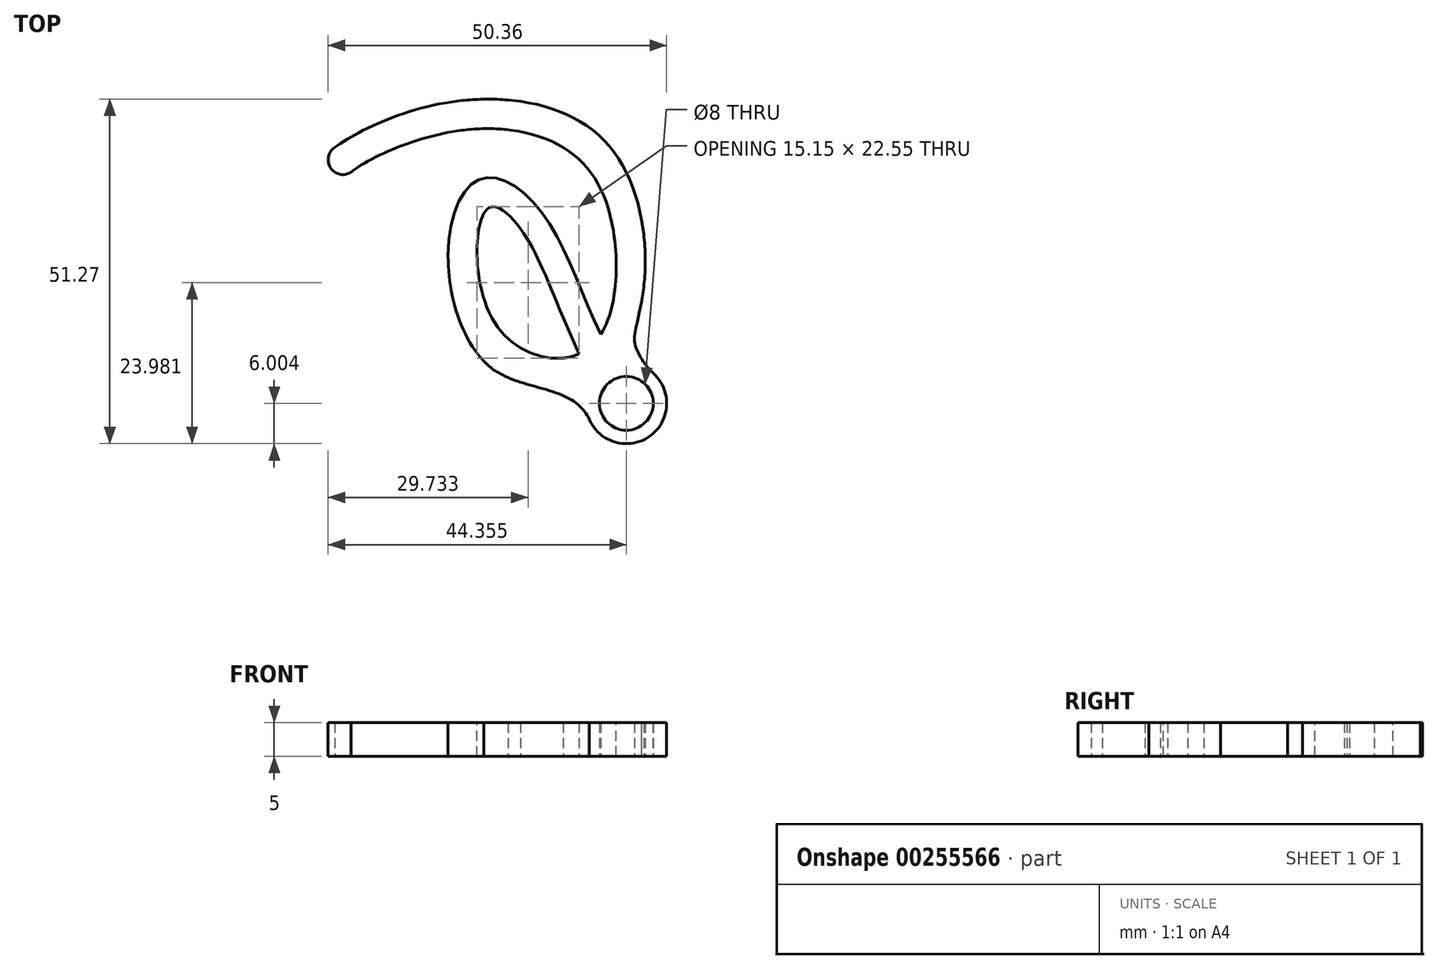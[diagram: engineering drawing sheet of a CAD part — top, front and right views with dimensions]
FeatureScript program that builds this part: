
annotation { "Feature Type Name" : "Feature", "Feature Type Description" : "" }
export const myFeature = defineFeature(function(context is Context, id is Id, definition is map)
    precondition{}
    {
        {
            var Q0;
            Q0=qCreatedBy(makeId("Front.planeOp"),FACE);
            var sketch = newSketch(context, id + "F0", { "sketchPlane" : qUnion([Q0])});
            skFitSpline(sketch, "E0", {"points": [v(-7.64, -32.72) * mm, v(-14.39, -18.66) * mm, v(-19.1, -15.72) * mm, v(-18.72, -31.73) * mm, v(-7.64, -37.97) * mm, v(-1.29, -32.33) * mm, v(-1.18, -15.7) * mm, v(-8.44, -6.5) * mm, v(-24.35, -4.3) * mm, v(-39.48, -10.34) * mm], "startDerivative": vector(-66.54, 155.96) * mm, "endDerivative": vector(-60.32, -50) * mm});
            skLineSegment(sketch, "E1", {"start": v(-8.07, -31.71) * mm, "end": v(-5.6, -37.39) * mm});
            skFitSpline(sketch, "E2", {"points": [v(-2.33, -34.44) * mm, v(-10.87, -16.7) * mm, v(-19.4, -11.15) * mm, v(-24.68, -18.43) * mm, v(-19.74, -38.45) * mm, v(-5, -41.52) * mm, v(3.68, -29.5) * mm, v(-1.85, -5.62) * mm, v(-25.4, 0) * mm, v(-41.93, -6.67) * mm], "startDerivative": vector(-78.74, 155.85) * mm, "endDerivative": vector(-78.56, -57.77) * mm});
            skLineSegment(sketch, "E3", {"start": v(-39.48, -10.34) * mm, "end": v(-41.93, -6.67) * mm});
            skCircle(sketch, "E4", {"center": v(-40.7, -8.5) * mm, "radius": 2.2 * mm});
            skSolve(sketch);
        }
        {
            var Q0;
            Q0=qCreatedBy(makeId("Top.planeOp"),FACE);
            var sketch = newSketch(context, id + "F1", { "sketchPlane" : qUnion([Q0])});
            skFitSpline(sketch, "E5", {"points": [v(14.78, -14.43) * mm, v(8.03, -0.37) * mm, v(3.33, 2.57) * mm, v(3.7, -13.44) * mm, v(14.78, -19.68) * mm, v(21.12, -14.03) * mm, v(21.16, 2.56) * mm, v(14.01, 11.88) * mm, v(-1.94, 13.98) * mm, v(-17.06, 7.95) * mm], "startDerivative": vector(-66.54, 155.96) * mm, "endDerivative": vector(-60.36, -49.94) * mm});
            skLineSegment(sketch, "E6", {"start": v(14.46, -13.68) * mm, "end": v(16.82, -19.1) * mm});
            skFitSpline(sketch, "E7", {"points": [v(20.09, -16.15) * mm, v(11.55, 1.6) * mm, v(3.01, 7.13) * mm, v(-2.26, -0.14) * mm, v(2.68, -20.15) * mm, v(17.42, -23.23) * mm, v(26.13, -11.2) * mm, v(20.6, 12.64) * mm, v(-3, 18.27) * mm, v(-19.5, 11.62) * mm], "startDerivative": vector(-78.74, 155.85) * mm, "endDerivative": vector(-78.48, -57.87) * mm});
            skLineSegment(sketch, "E8", {"start": v(-17.06, 7.95) * mm, "end": v(-19.5, 11.62) * mm});
            skCircle(sketch, "E9", {"center": v(-18.28, 9.79) * mm, "radius": 2.2 * mm});
            skLineSegment(sketch, "E10", {"start": v(4, 2.8) * mm, "end": v(13.82, -19.75) * mm});
            skLineSegment(sketch, "E11", {"start": v(-3, 18.27) * mm, "end": v(-1.94, 13.98) * mm});
            skLineSegment(sketch, "E12", {"start": v(6.27, 18.68) * mm, "end": v(8.13, 18.47) * mm});
            skLineSegment(sketch, "E13", {"start": v(7.2, 18.58) * mm, "end": v(6.7, 14.2) * mm});
            skLineSegment(sketch, "E14", {"start": v(26.1, 0.98) * mm, "end": v(26.45, -1.27) * mm});
            skLineSegment(sketch, "E15", {"start": v(26.3, -0.15) * mm, "end": v(21.94, -0.82) * mm});
            skPoint(sketch, "E15.startSnap0", {"position": v(26.28, -0.15) * mm});
            skLineSegment(sketch, "E16", {"start": v(16.82, -19.1) * mm, "end": v(18.42, -22.8) * mm});
            skLineSegment(sketch, "E17", {"start": v(-17.06, 7.95) * mm, "end": v(18.42, -22.8) * mm});
            skLineSegment(sketch, "E18", {"start": v(20.09, -16.15) * mm, "end": v(21.87, -20.23) * mm});
            skLineSegment(sketch, "E19", {"start": v(20.28, -21.64) * mm, "end": v(23.87, -26.46) * mm});
            skCircle(sketch, "E20", {"center": v(23.87, -26.46) * mm, "radius": 6 * mm});
            skFitSpline(sketch, "E21", {"points": [v(2.68, -20.15) * mm, v(13.87, -25.05) * mm, v(18.35, -28.82) * mm], "startDerivative": vector(13.57, -15.72) * mm, "endDerivative": vector(5.37, -11.86) * mm});
            skFitSpline(sketch, "E22", {"points": [v(27.79, -21.92) * mm, v(25.16, -17.6) * mm, v(26.13, -11.2) * mm], "startDerivative": vector(-9.12, 8.94) * mm, "endDerivative": vector(4.13, 22.33) * mm});
            skCircle(sketch, "E23", {"center": v(23.87, -26.46) * mm, "radius": 4 * mm});
            skSolve(sketch);
        }
        {
            var Q0;
            {var subQ0=sQuery(id+"F1.wireOp",EDGE,"E8");Q0=makeQuery(id+"F1.imprint","IMPRINT",FACE,{"disambiguationData":[TD([[makeQuery(id+"F1.imprint","IMPRINT",EDGE,{"derivedFrom":subQ0}),1.0]])]});}
            var Q1;
            {var subQ1=sQuery(id+"F1.wireOp",EDGE,"E8");Q1=makeQuery(id+"F1.imprint","IMPRINT",FACE,{"disambiguationData":[TD([[makeQuery(id+"F1.imprint","IMPRINT",EDGE,{"derivedFrom":subQ1}),-1.0]])]});}
            var Q2;
            {var subQ0=sQuery(id+"F1.wireOp",EDGE,"E11");Q2=makeQuery(id+"F1.imprint","IMPRINT",FACE,{"disambiguationData":[TD([[makeQuery(id+"F1.imprint","IMPRINT",EDGE,{"derivedFrom":subQ0}),-1.0]])]});}
            var Q3;
            {var subQ4=sQuery(id+"F1.wireOp",EDGE,"E11");Q3=makeQuery(id+"F1.imprint","IMPRINT",FACE,{"disambiguationData":[TD([[makeQuery(id+"F1.imprint","IMPRINT",EDGE,{"derivedFrom":subQ4}),1.0]])]});}
            var Q4;
            {var subQ0=sQuery(id+"F1.wireOp",EDGE,"E13");Q4=makeQuery(id+"F1.imprint","IMPRINT",FACE,{"disambiguationData":[TD([[makeQuery(id+"F1.imprint","IMPRINT",EDGE,{"derivedFrom":subQ0}),1.0]])]});}
            var Q5;
            {var subQ6=sQuery(id+"F1.wireOp",EDGE,"E18");Q5=makeQuery(id+"F1.imprint","IMPRINT",FACE,{"disambiguationData":[TD([[makeQuery(id+"F1.imprint","IMPRINT",EDGE,{"derivedFrom":subQ6}),1.0]])]});}
            var Q6;
            {var subQ0=sQuery(id+"F1.wireOp",EDGE,"E19");var subQ1=sQuery(id+"F1.wireOp",EDGE,"E7");var subQ2=makeQuery(id+"F1.imprint","INTERSECT",VERTEX,{"derivedFrom":[subQ1,subQ0]});Q6=makeQuery(id+"F1.imprint","IMPRINT",FACE,{"disambiguationData":[TD([[makeQuery(id+"F1.imprint","IMPRINT",EDGE,{"disambiguationData":[TD([[subQ2,-1.0]])],"derivedFrom":subQ1}),1.0]])]});}
            var Q7;
            Q7=makeQuery(id+"F1.imprint","IMPRINT",FACE,{"disambiguationData":[TD([[makeQuery(id+"F1.imprint","IMPRINT",EDGE,{"derivedFrom":sQuery(id+"F1.wireOp",EDGE,"E23")}),-1.0]])]});
            var Q8;
            {var subQ0=sQuery(id+"F1.wireOp",EDGE,"E19");var subQ1=sQuery(id+"F1.wireOp",EDGE,"E7");var subQ2=makeQuery(id+"F1.imprint","INTERSECT",VERTEX,{"derivedFrom":[subQ1,subQ0]});Q8=makeQuery(id+"F1.imprint","IMPRINT",FACE,{"disambiguationData":[TD([[makeQuery(id+"F1.imprint","IMPRINT",EDGE,{"disambiguationData":[TD([[subQ2,1.0]])],"derivedFrom":subQ1}),1.0]])]});}
            var Q9;
            {var subQ4=sQuery(id+"F1.wireOp",EDGE,"E22");Q9=makeQuery(id+"F1.imprint","IMPRINT",FACE,{"disambiguationData":[TD([[makeQuery(id+"F1.imprint","IMPRINT",EDGE,{"derivedFrom":subQ4}),1.0]])]});}
            var Q10;
            {var subQ0=sQuery(id+"F1.wireOp",EDGE,"E16");Q10=makeQuery(id+"F1.imprint","IMPRINT",FACE,{"disambiguationData":[TD([[makeQuery(id+"F1.imprint","IMPRINT",EDGE,{"derivedFrom":subQ0}),1.0]])]});}
            var Q11;
            {var subQ0=sQuery(id+"F1.wireOp",EDGE,"E6");Q11=makeQuery(id+"F1.imprint","IMPRINT",FACE,{"disambiguationData":[TD([[makeQuery(id+"F1.imprint","IMPRINT",EDGE,{"derivedFrom":subQ0}),1.0]])]});}
            var Q12;
            {var subQ4=sQuery(id+"F1.wireOp",EDGE,"E5");var subQ5=makeQuery(id+"F1.imprint","INTERSECT",VERTEX,{"disambiguationData":[OD(1.0)],"derivedFrom":[subQ4,sQuery(id+"F1.wireOp",EDGE,"E10")]});Q12=makeQuery(id+"F1.imprint","IMPRINT",FACE,{"disambiguationData":[TD([[makeQuery(id+"F1.imprint","IMPRINT",EDGE,{"disambiguationData":[TD([[subQ5,1.0]])],"derivedFrom":subQ4}),-1.0]])]});}
            var Q13;
            {var subQ2=sQuery(id+"F1.wireOp",EDGE,"E21");Q13=makeQuery(id+"F1.imprint","IMPRINT",FACE,{"disambiguationData":[TD([[makeQuery(id+"F1.imprint","IMPRINT",EDGE,{"derivedFrom":subQ2}),1.0]])]});}
            var Q14;
            {var subQ0=sQuery(id+"F1.wireOp",EDGE,"E16");Q14=makeQuery(id+"F1.imprint","IMPRINT",FACE,{"disambiguationData":[TD([[makeQuery(id+"F1.imprint","IMPRINT",EDGE,{"derivedFrom":subQ0}),-1.0]])]});}
            extrude(context, id + "F2", {"entities" : qUnion([Q0, Q1, Q2, Q3, Q4, Q5, Q6, Q7, Q8, Q9, Q10, Q11, Q12, Q13, Q14]), "depth" : 5 * mm});
        }
        {
            var Q0;
            {var subQ2=sQuery(id+"F1.wireOp",EDGE,"E21");var subQ4=sQuery(id+"F1.wireOp",EDGE,"E20");var subQ6=makeQuery(id+"F1.imprint","INTERSECT",VERTEX,{"derivedFrom":[subQ4,subQ2]});Q0=makeQuery(id+"F1.imprint","IMPRINT",FACE,{"disambiguationData":[TD([[makeQuery(id+"F1.imprint","IMPRINT",EDGE,{"disambiguationData":[TD([[subQ6,1.0]])],"derivedFrom":subQ4}),-1.0]])]});}
            extrude(context, id + "F3", {"entities" : qUnion([Q0]), "operationType" : NewBodyOperationType.ADD, "depth" : 5 * mm, "offsetDistance" : 25 * mm});
        }
    });
